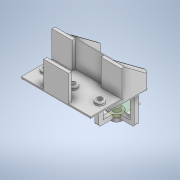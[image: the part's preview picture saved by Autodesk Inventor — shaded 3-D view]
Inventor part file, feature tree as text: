
AUTODESK INVENTOR PART (.ipt)
format: ipt  version: 2020 (Build 240168000, 168)  size: 542,208 bytes
history: native  units: in
note: dims shown in document units (in); Inventor stores cm internally (conversion verified against a paired STEP export)
features: sketch x27, extrude x26, fillet x4, plane x1, chamfer x1, mirror x1
ambient origin geometry x8: Origin, YZ Plane, XZ Plane, XY Plane, X Axis, Y Axis, Z Axis, Center Point
bodies: Solid1 (feature_tree)
feature tree (60):
  extrude  "Extrusion1"  Depth=1.2756in
  extrude  "Extrusion3"  Depth=0.1181in
  extrude  "Extrusion4"  Depth=0.1181in TaperAngle=0.0deg
  extrude  "Extrusion5"  Depth=0.1181in TaperAngle=0.0deg
  extrude  "Extrusion6"  Depth=0.1181in TaperAngle=0.0deg
  extrude  "Extrusion9"  Depth=0.3346in
  extrude  "Extrusion10"  Depth=0.1181in
  extrude  "Extrusion11"  Depth=0.2953in
  extrude  "Extrusion14"  Depth=0.3346in
  extrude  "Extrusion16"  Depth=0.1181in
  sketch  "Sketch17"  dims[d41=0.1181in d42=1.0in d43=0.0in]
  extrude  "Extrusion17"  Depth=0.1181in TaperAngle=0.0deg
  extrude  "Extrusion18"  Depth=0.2362in
  extrude  "Extrusion20"  Depth=0.2362in
  extrude  "Extrusion21"  Depth=0.1181in
  extrude  "Extrusion22"  Depth=0.1969in
  extrude  "Extrusion25"  Depth=0.1969in
  extrude  "Extrusion26"  Depth=0.1575in
  extrude  "Extrusion27"  Depth=0.1181in
  extrude  "Extrusion28"  Depth=0.1181in
  extrude  "Extrusion29"  Depth=1.9685in TaperAngle=0.0deg
  plane  "Work Plane1"
  extrude  "Extrusion30"  Depth=0.4724in
  chamfer  "Chamfer1"  Distance=0.2362in
  mirror  "Mirror1"
  fillet  "Fillet4"  Radius=0.1575in
  fillet  "Fillet5"  Radius=0.1575in
  extrude  "Extrusion31"  Depth=0.0591in
  extrude  "Extrusion32"  Depth=0.0591in
  extrude  "Extrusion33"  Depth=0.0591in
  extrude  "Extrusion34"  Depth=0.0591in
  fillet  "Fillet6"  Radius=0.9055in
  extrude  "Extrusion35"  Depth=0.0591in
  fillet  "Fillet7"  Radius=0.1575in
  sketch  "Sketch1"  dims[d0=1.6142in d1=1.2756in]
  sketch  "Sketch3"  dims[d2=0.1181in d3=0.0in d8=0.1181in]
  sketch  "Sketch4"  dims[d9=0.1181in d10=1.0in d11=0.0in]
  sketch  "Sketch5"  dims[d12=0.8465in d13=0.1181in d14=0.0in]
  sketch  "Sketch6"  dims[d15=0.8465in d16=0.1181in d17=0.0in]
  sketch  "Sketch9"  dims[d20=0.3346in d21=0.3346in]
  sketch  "Sketch10"  dims[d22=0.1181in d23=0.0in d32=1.0236in]
  sketch  "Sketch11"  dims[d33=0.2953in d34=0.2953in]
  sketch  "Sketch14"  dims[d35=1.0236in d36=0.0in d37=0.3346in]
  sketch  "Sketch16"  dims[d38=0.1181in d39=0.0in d40=0.7677in]
  sketch  "Sketch18"  dims[d50=0.1772in d51=0.0in d59=0.2362in]
  sketch  "Sketch19"  dims[d60=0.2362in d61=0.2362in]
  sketch  "Sketch21"  dims[d62=0.1181in d63=0.0in d64=1.9291in]
  sketch  "Sketch22"  dims[d65=0.1969in d66=0.1969in]
  sketch  "Sketch23"  dims[d67=0.1969in d68=0.1969in]
  sketch  "Sketch26"  dims[d69=0.4724in d70=0.0in d71=0.1575in]
  sketch  "Sketch27"  dims[d72=0.1181in d73=0.1181in]
  sketch  "Sketch28"  dims[d74=1.9291in d75=0.0in d78=0.1181in]
  sketch  "Sketch29"  dims[d79=1.4331in d80=0.0in d81=1.9685in d82=0.0in]
  sketch  "Sketch30"  dims[d83=1.9685in d84=0.0in d103=0.4724in]
  sketch  "Sketch31"  dims[d104=0.1575in]
  sketch  "Sketch32"  dims[d105=0.6693in]
  sketch  "Sketch33"  dims[d106=0.6693in]
  sketch  "Sketch34"  dims[d107=0.1575in]
  sketch  "Sketch35"  dims[d108=0.6693in]
  sketch  "Sketch36"  dims[d109=0.1575in d111=0.2362in d112=0.0in d113=0.1575in d114=0.1575in d115=0.1575in d116=0.1575in d117=0.1575in d118=0.1575in d119=0.9055in d120=0.0in d121=0.1575in d122=0.1575in d123=1.2598in d124=0.0in d125=0.1575in d126=0.1575in d127=0.6299in d128=0.0in d129=0.4724in d130=0.1575in d131=0.0in d132=0.374in d133=0.2756in d134=0.1772in d135=0.0in d136=0.0394in d137=0.0787in d138=45.0deg d139=0.0787in d140=0.0591in d141=0.2165in d142=0.1575in d143=1.5748in d144=0.0in d145=0.2362in d146=0.3937in d147=0.1181in d148=0.0787in d149=0.0in d150=0.0in d151=0.2362in d152=0.3937in d153=0.1181in d154=0.0in d155=0.7046in d156=1.1811in d157=0.0in d158=0.0591in d159=0.1575in d160=0.1575in d161=0.1575in d162=1.1811in d163=0.0in d164=0.0591in d44=0.0197in d45=0.0344in]
